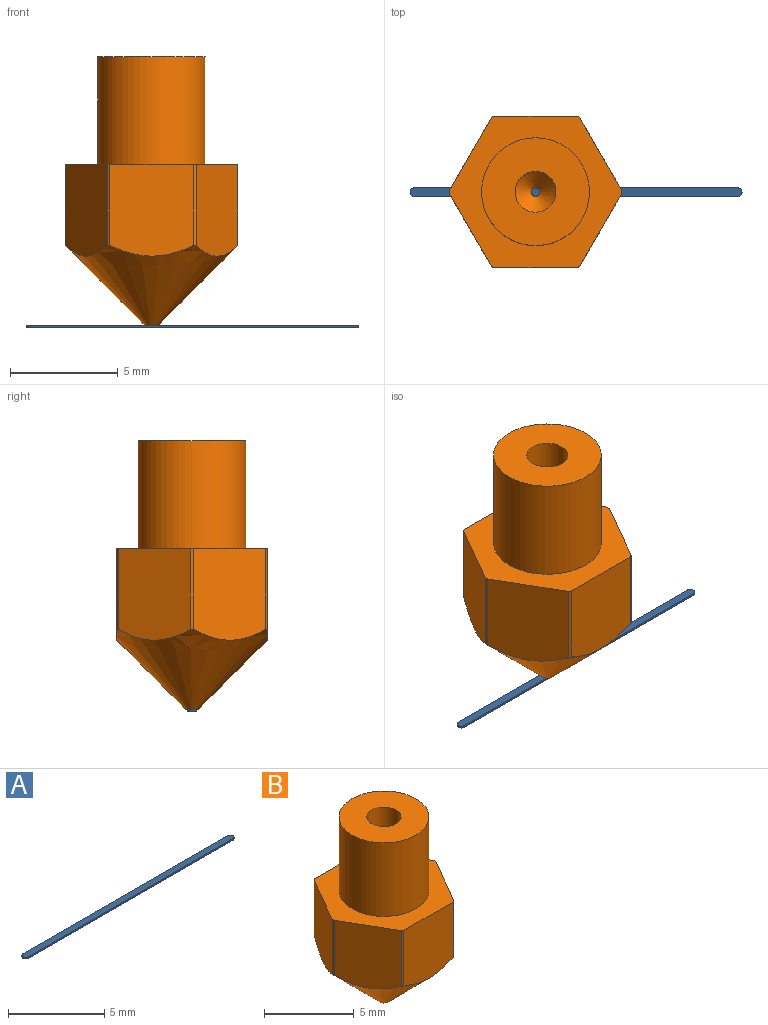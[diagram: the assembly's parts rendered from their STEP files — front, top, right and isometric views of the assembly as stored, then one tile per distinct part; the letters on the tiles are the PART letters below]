
ASSEMBLY  parts=2 mates=2
PART A: 6 faces, bbox 15.4x0.4x0.1 mm
  f0: plane 15x0.1mm, normal (0,1,0), area 1.5mm2, adj f1,f3,f4,f5
  f1: cylinder r=0.2mm len=0.4mm, axis (0,0,-1), area 0.1mm2, adj f0,f2,f4,f5
  f2: plane 15x0.1mm, normal (0,-1,0), area 1.5mm2, adj f1,f3,f4,f5
  f3: cylinder r=0.2mm len=0.4mm, axis (0,0,-1), area 0.1mm2, adj f0,f2,f4,f5
  f4: plane 15.4x0.4mm, normal (0,0,1), area 6.1mm2, adj f0,f1,f2,f3
  f5: plane 15.4x0.4mm, normal (0,0,-1), area 6.1mm2, adj f0,f1,f2,f3
PART B: 20 faces, bbox 8x8x12.5 mm
  f0: cylinder r=4mm len=3.75mm, axis (0,0,-1), area 0.5mm2, adj f6,f7,f18,f19
  f1: cylinder r=4mm len=3.75mm, axis (0,0,-1), area 0.5mm2, adj f6,f7,f14,f19
  f2: cylinder r=4mm len=3.75mm, axis (0,0,-1), area 0.5mm2, adj f6,f7,f17,f18
  f3: cylinder r=4mm len=3.75mm, axis (0,0,-1), area 0.5mm2, adj f6,f7,f16,f17
  f4: cylinder r=4mm len=3.75mm, axis (0,0,-1), area 0.5mm2, adj f6,f7,f15,f16
  f5: cylinder r=4mm len=3.75mm, axis (0,0,-1), area 0.5mm2, adj f6,f7,f14,f15
  f6: cone r=4mm half-angle=45deg, axis (0,0,1), area 59.6mm2, adj f0,f1,f2,f3,f4,f5,f8,f14
  f7: plane 8x7mm, normal (0,0,1), area 22.8mm2, adj f0,f1,f2,f3,f4,f5,f13,f14
  f8: plane 0.6x0.6mm, normal (0,0,-1), area 0.2mm2, adj f6,f9
  f9: cylinder r=0.2mm len=0.7mm, axis (0,0,-1), area 0.9mm2, adj f8,f10
  f10: cone r=0.2mm half-angle=45deg, axis (0,0,1), area 3.8mm2, adj f9,f11
  f11: cylinder r=0.95mm len=11mm, axis (0,0,-1), area 65.7mm2, adj f10,f12
  f12: plane 5x5mm, normal (0,0,1), area 16.8mm2, adj f11,f13
  f13: cylinder r=2.5mm len=5mm, axis (0,0,-1), area 78.5mm2, adj f7,f12
  f14: plane 4.26x3.36mm, normal (-0.87,0.5,0), area 15.8mm2, adj f1,f5,f6,f7
  f15: plane 4.26x3.36mm, normal (-0.87,-0.5,0), area 15.8mm2, adj f4,f5,f6,f7
  f16: plane 4.26x3.88mm, normal (0,-1,0), area 15.8mm2, adj f3,f4,f6,f7
  f17: plane 4.26x3.36mm, normal (0.87,-0.5,0), area 15.8mm2, adj f2,f3,f6,f7
  f18: plane 4.26x3.36mm, normal (0.87,0.5,0), area 15.8mm2, adj f0,f2,f6,f7
  f19: plane 4.26x3.88mm, normal (0,1,0), area 15.8mm2, adj f0,f1,f6,f7
PLACE A t=(0,0,-0.1)mm
PLACE B t=(5.62,0,0)mm
MATE pin_slot B.f0 <-> A.f4  axis (0,0,1) through (5.62,0,0)mm
MATE parallel B.f16 <-> A.f2  axis (0,-1,0) through (5.62,-3.5,5.41)mm
